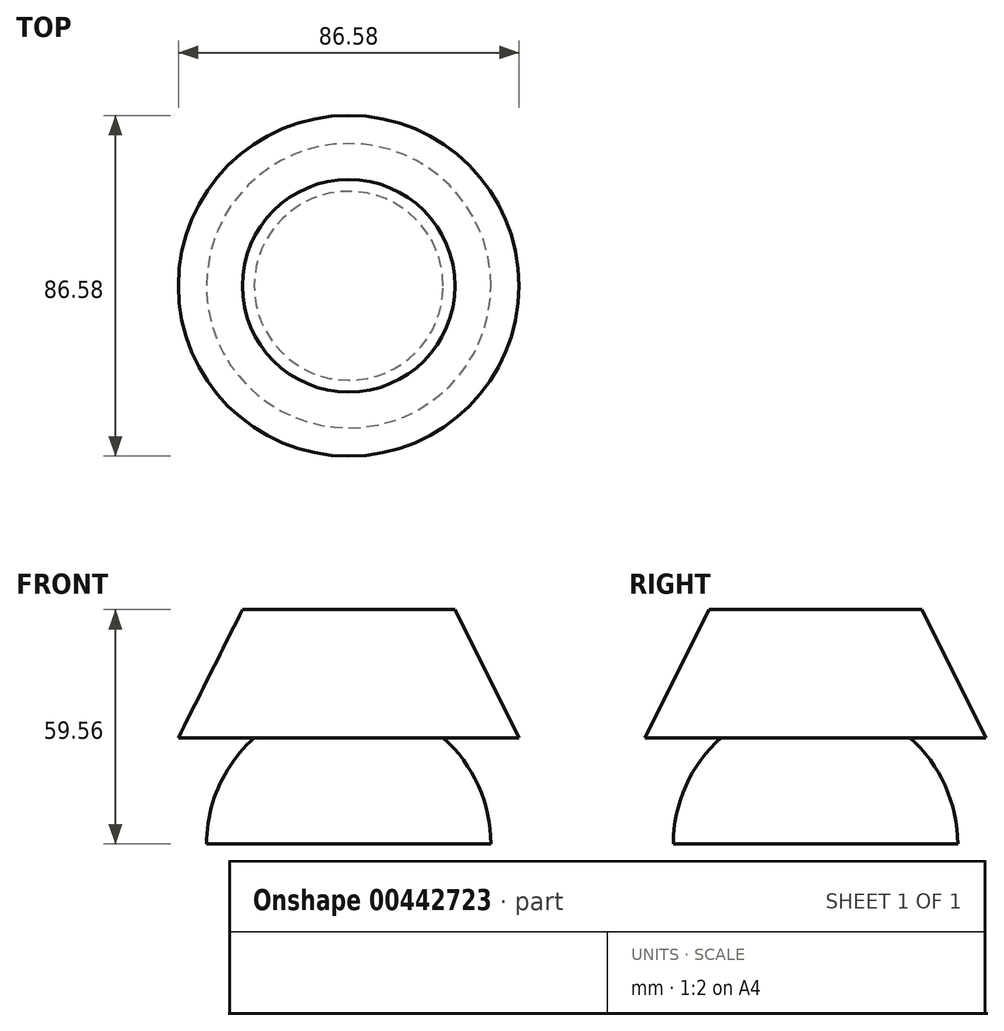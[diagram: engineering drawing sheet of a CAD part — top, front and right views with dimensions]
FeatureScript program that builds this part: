
annotation { "Feature Type Name" : "Feature", "Feature Type Description" : "" }
export const myFeature = defineFeature(function(context is Context, id is Id, definition is map)
    precondition{}
    {
        {
            var Q0;
            Q0=qCreatedBy(makeId("Front.planeOp"),FACE);
            var sketch = newSketch(context, id + "F0", { "sketchPlane" : qUnion([Q0])});
            skLineSegment(sketch, "E0", {"start": v(0, 59.56) * mm, "end": v(-27, 59.56) * mm});
            skLineSegment(sketch, "E1", {"start": v(-27, 59.56) * mm, "end": v(-43.29, 27) * mm});
            skLineSegment(sketch, "E2", {"start": v(-43.29, 27) * mm, "end": v(-24, 27) * mm});
            skLineSegment(sketch, "E3", {"start": v(0, 27) * mm, "end": v(0, 59.56) * mm});
            skArc(sketch, "E4", {"start": v(-24, 27) * mm, "mid": v(-32.96, 14.8) * mm, "end": v(-36.13, 0) * mm});
            skLineSegment(sketch, "E5", {"start": v(0, 0) * mm, "end": v(-36.13, 0) * mm});
            skLineSegment(sketch, "E6", {"start": v(0, 27) * mm, "end": v(0, 0) * mm});
            skSolve(sketch);
        }
        {
            var Q0;
            Q0=makeQuery(id+"F0.imprint","IMPRINT",FACE,{"disambiguationData":[TD([[makeQuery(id+"F0.imprint","IMPRINT",EDGE,{"derivedFrom":sQuery(id+"F0.wireOp",EDGE,"E0")}),1.0]])]});
            var Q1;
            Q1=sQuery(id+"F0.wireOp",EDGE,"E3");
            revolve(context, id + "F1", {"entities" : qUnion([Q0]), "axis" : qUnion([Q1]), "revolveType" : RevolveType.FULL});
        }
    });
